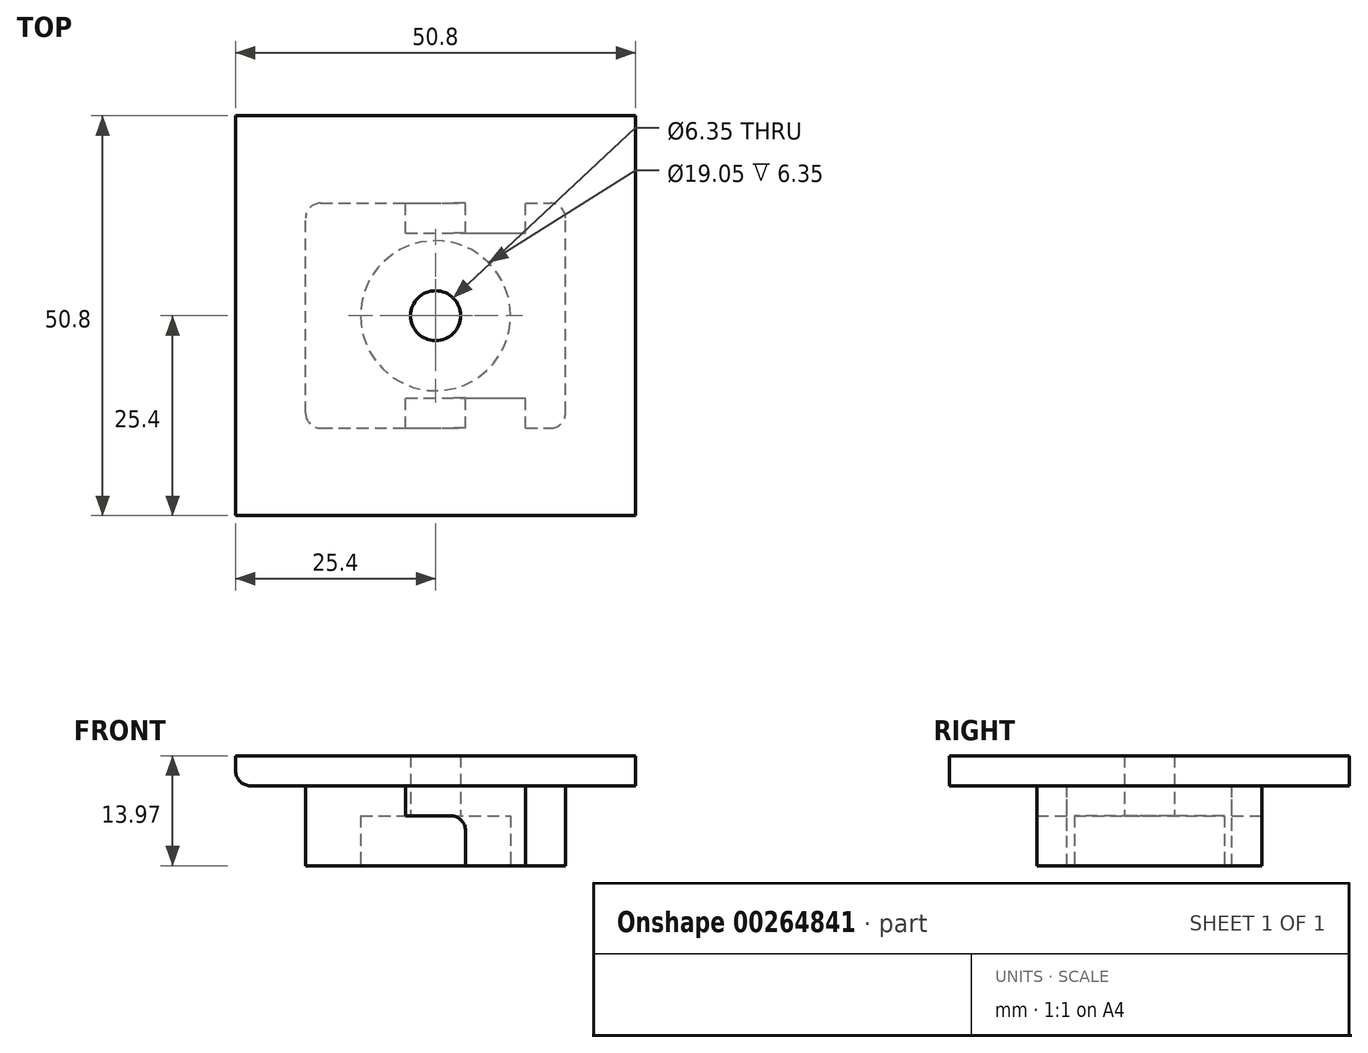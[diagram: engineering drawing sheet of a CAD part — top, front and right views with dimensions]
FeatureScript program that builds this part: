
annotation { "Feature Type Name" : "Feature", "Feature Type Description" : "" }
export const myFeature = defineFeature(function(context is Context, id is Id, definition is map)
    precondition{}
    {
        {
            var Q0;
            Q0=qCreatedBy(makeId("Top.planeOp"),FACE);
            var sketch = newSketch(context, id + "F0", { "sketchPlane" : qUnion([Q0])});
            skLineSegment(sketch, "E0.bottom", {"start": v(-25.4, 25.4) * mm, "end": v(25.4, 25.4) * mm});
            skLineSegment(sketch, "E0.top", {"start": v(-25.4, -25.4) * mm, "end": v(25.4, -25.4) * mm});
            skLineSegment(sketch, "E0.left", {"start": v(-25.4, 25.4) * mm, "end": v(-25.4, -25.4) * mm});
            skLineSegment(sketch, "E0.right", {"start": v(25.4, 25.4) * mm, "end": v(25.4, -25.4) * mm});
            skLineSegment(sketch, "E1", {"start": v(-25.4, 0) * mm, "end": v(25.4, 0) * mm, "construction": true});
            skSolve(sketch);
        }
        {
            var Q0;
            Q0 = qSketchRegion(id + "F0", true);
            extrude(context, id + "F1", {"entities" : qUnion([Q0]), "depth" : 3.8 * mm});
        }
        {
            var Q0;
            Q0=makeQuery(id+"F1.opExtrude","CAP_FACE",FACE,{"disambiguationData":[OSD([sQuery(id+"F0.wireOp",EDGE,"E0.bottom"),sQuery(id+"F0.wireOp",EDGE,"E0.top"),sQuery(id+"F0.wireOp",EDGE,"E0.left"),sQuery(id+"F0.wireOp",EDGE,"E0.right")])],"isStart":true});
            var sketch = newSketch(context, id + "F2", { "sketchPlane" : qUnion([Q0])});
            skLineSegment(sketch, "E2.bottom", {"start": v(-16.51, 14.29) * mm, "end": v(-3.81, 14.29) * mm});
            skLineSegment(sketch, "E2.top", {"start": v(-16.51, -14.29) * mm, "end": v(-3.81, -14.29) * mm});
            skLineSegment(sketch, "E2.left", {"start": v(-16.51, 14.29) * mm, "end": v(-16.51, -14.29) * mm});
            skLineSegment(sketch, "E2.right", {"start": v(16.51, 14.29) * mm, "end": v(16.51, -14.29) * mm});
            skLineSegment(sketch, "E3", {"start": v(-16.51, 0) * mm, "end": v(16.51, 0) * mm, "construction": true});
            skLineSegment(sketch, "E4", {"start": v(11.43, 14.29) * mm, "end": v(11.43, 10.48) * mm});
            skLineSegment(sketch, "E5", {"start": v(-3.81, 14.29) * mm, "end": v(-3.81, 10.48) * mm});
            skLineSegment(sketch, "E6", {"start": v(-3.81, 10.48) * mm, "end": v(11.43, 10.48) * mm});
            skLineSegment(sketch, "E7", {"start": v(-3.81, -10.48) * mm, "end": v(11.43, -10.48) * mm});
            skLineSegment(sketch, "E8.trimOffspring", {"start": v(-3.81, -10.48) * mm, "end": v(-3.81, -14.29) * mm});
            skLineSegment(sketch, "E9.trimOffspring", {"start": v(11.43, -10.48) * mm, "end": v(11.43, -14.29) * mm});
            skLineSegment(sketch, "E10.trimOffspring", {"start": v(11.43, -14.29) * mm, "end": v(16.51, -14.29) * mm});
            skLineSegment(sketch, "E11.trimOffspring", {"start": v(11.43, 14.29) * mm, "end": v(16.51, 14.29) * mm});
            skSolve(sketch);
        }
        {
            var Q0;
            Q0 = qSketchRegion(id + "F2", true);
            extrude(context, id + "F3", {"entities" : qUnion([Q0]), "operationType" : NewBodyOperationType.ADD, "depth" : 3.8 * mm});
        }
        {
            var Q0;
            Q0=makeQuery(id+"F3.opExtrude","CAP_FACE",FACE,{"disambiguationData":[OSD([sQuery(id+"F2.wireOp",EDGE,"E2.bottom"),sQuery(id+"F2.wireOp",EDGE,"E2.top"),sQuery(id+"F2.wireOp",EDGE,"E2.left"),sQuery(id+"F2.wireOp",EDGE,"E2.right"),sQuery(id+"F2.wireOp",EDGE,"E4"),sQuery(id+"F2.wireOp",EDGE,"E5"),sQuery(id+"F2.wireOp",EDGE,"E6"),sQuery(id+"F2.wireOp",EDGE,"E7"),sQuery(id+"F2.wireOp",EDGE,"E8.trimOffspring"),sQuery(id+"F2.wireOp",EDGE,"E9.trimOffspring"),sQuery(id+"F2.wireOp",EDGE,"E10.trimOffspring"),sQuery(id+"F2.wireOp",EDGE,"E11.trimOffspring")])],"isStart":false});
            var sketch = newSketch(context, id + "F4", { "sketchPlane" : qUnion([Q0])});
            skLineSegment(sketch, "E12.bottom", {"start": v(-16.51, 14.29) * mm, "end": v(3.81, 14.29) * mm});
            skLineSegment(sketch, "E12.top", {"start": v(-16.51, -14.29) * mm, "end": v(3.81, -14.29) * mm});
            skLineSegment(sketch, "E12.left", {"start": v(-16.51, 14.29) * mm, "end": v(-16.51, -14.29) * mm});
            skLineSegment(sketch, "E12.right", {"start": v(16.51, 14.29) * mm, "end": v(16.51, -14.29) * mm});
            skLineSegment(sketch, "E13", {"start": v(3.81, 14.29) * mm, "end": v(3.81, 10.48) * mm});
            skPoint(sketch, "E13.endSnap0", {"position": v(0, -14.29) * mm});
            skLineSegment(sketch, "E14", {"start": v(3.81, 10.48) * mm, "end": v(11.43, 10.48) * mm});
            skLineSegment(sketch, "E15", {"start": v(11.43, 10.48) * mm, "end": v(11.43, 14.29) * mm});
            skLineSegment(sketch, "E16", {"start": v(3.81, -10.48) * mm, "end": v(11.43, -10.48) * mm});
            skLineSegment(sketch, "E17", {"start": v(11.43, -10.48) * mm, "end": v(11.43, -14.29) * mm});
            skLineSegment(sketch, "E18.trimOffspring", {"start": v(11.43, 14.29) * mm, "end": v(16.51, 14.29) * mm});
            skLineSegment(sketch, "E19.trimOffspring", {"start": v(3.81, -10.48) * mm, "end": v(3.81, -14.29) * mm});
            skLineSegment(sketch, "E20.trimOffspring", {"start": v(11.43, -14.29) * mm, "end": v(16.51, -14.29) * mm});
            skSolve(sketch);
        }
        {
            var Q0;
            Q0 = qSketchRegion(id + "F4", true);
            extrude(context, id + "F5", {"entities" : qUnion([Q0]), "operationType" : NewBodyOperationType.ADD, "depth" : 6.35 * mm});
        }
        {
            var Q0;
            Q0=makeQuery(id+"F5.opExtrude","CAP_EDGE",EDGE,{"disambiguationData":[OSD([sQuery(id+"F4.wireOp",EDGE,"E13")])],"isStart":true});
            var Q1;
            Q1=makeQuery(id+"F5.boolean.opBoolean","MERGE",EDGE,{"derivedFrom":[makeQuery(id+"F3.opExtrude","SWEPT_EDGE",EDGE,{"disambiguationData":[OSD([sQuery(id+"F2.wireOp",EDGE,"E2.right"),sQuery(id+"F2.wireOp",EDGE,"E11.trimOffspring")])]}),makeQuery(id+"F5.opExtrude","SWEPT_EDGE",EDGE,{"disambiguationData":[OSD([sQuery(id+"F4.wireOp",EDGE,"E12.right"),sQuery(id+"F4.wireOp",EDGE,"E18.trimOffspring")])]})]});
            var Q2;
            Q2=makeQuery(id+"F5.boolean.opBoolean","MERGE",EDGE,{"derivedFrom":[makeQuery(id+"F3.opExtrude","SWEPT_EDGE",EDGE,{"disambiguationData":[OSD([sQuery(id+"F2.wireOp",EDGE,"E2.right"),sQuery(id+"F2.wireOp",EDGE,"E10.trimOffspring")])]}),makeQuery(id+"F5.opExtrude","SWEPT_EDGE",EDGE,{"disambiguationData":[OSD([sQuery(id+"F4.wireOp",EDGE,"E12.right"),sQuery(id+"F4.wireOp",EDGE,"E20.trimOffspring")])]})]});
            var Q3;
            Q3=makeQuery(id+"F5.opExtrude","CAP_EDGE",EDGE,{"disambiguationData":[OSD([sQuery(id+"F4.wireOp",EDGE,"E19.trimOffspring")])],"isStart":true});
            var Q4;
            Q4=makeQuery(id+"F5.boolean.opBoolean","MERGE",EDGE,{"derivedFrom":[makeQuery(id+"F3.opExtrude","SWEPT_EDGE",EDGE,{"disambiguationData":[OSD([sQuery(id+"F2.wireOp",EDGE,"E2.top"),sQuery(id+"F2.wireOp",EDGE,"E2.left")])]}),makeQuery(id+"F5.opExtrude","SWEPT_EDGE",EDGE,{"disambiguationData":[OSD([sQuery(id+"F4.wireOp",EDGE,"E12.top"),sQuery(id+"F4.wireOp",EDGE,"E12.left")])]})]});
            var Q5;
            Q5=makeQuery(id+"F5.boolean.opBoolean","MERGE",EDGE,{"derivedFrom":[makeQuery(id+"F3.opExtrude","SWEPT_EDGE",EDGE,{"disambiguationData":[OSD([sQuery(id+"F2.wireOp",EDGE,"E2.bottom"),sQuery(id+"F2.wireOp",EDGE,"E2.left")])]}),makeQuery(id+"F5.opExtrude","SWEPT_EDGE",EDGE,{"disambiguationData":[OSD([sQuery(id+"F4.wireOp",EDGE,"E12.bottom"),sQuery(id+"F4.wireOp",EDGE,"E12.left")])]})]});
            var Q6;
            Q6=makeQuery(id+"F1.opExtrude","CAP_EDGE",EDGE,{"disambiguationData":[OSD([sQuery(id+"F0.wireOp",EDGE,"E0.left")])],"isStart":true});
            fillet(context, id + "F6", {"entities" : qUnion([Q0, Q1, Q2, Q3, Q4, Q5, Q6]), "radius" : 1.9 * mm, "allowEdgeOverflow" : false});
        }
        {
            var Q0;
            Q0=makeQuery(id+"F5.opExtrude","CAP_FACE",FACE,{"disambiguationData":[OSD([sQuery(id+"F4.wireOp",EDGE,"E12.bottom"),sQuery(id+"F4.wireOp",EDGE,"E12.top"),sQuery(id+"F4.wireOp",EDGE,"E12.left"),sQuery(id+"F4.wireOp",EDGE,"E12.right"),sQuery(id+"F4.wireOp",EDGE,"E13"),sQuery(id+"F4.wireOp",EDGE,"E14"),sQuery(id+"F4.wireOp",EDGE,"E15"),sQuery(id+"F4.wireOp",EDGE,"E16"),sQuery(id+"F4.wireOp",EDGE,"E17"),sQuery(id+"F4.wireOp",EDGE,"E18.trimOffspring"),sQuery(id+"F4.wireOp",EDGE,"E19.trimOffspring"),sQuery(id+"F4.wireOp",EDGE,"E20.trimOffspring")])],"isStart":false});
            var sketch = newSketch(context, id + "F7", { "sketchPlane" : qUnion([Q0])});
            skPoint(sketch, "E21", {"position": v(0, 0) * mm});
            skSolve(sketch);
        }
        {
            var Q0;
            Q0=sQuery(id+"F7.wireOp",VERTEX,"E21");
            var Q1;
            Q1=makeQuery(id+"F1.opExtrude","SWEPT_BODY",BODY,{"disambiguationData":[OSD([sQuery(id+"F0.wireOp",EDGE,"E0.bottom"),sQuery(id+"F0.wireOp",EDGE,"E0.top"),sQuery(id+"F0.wireOp",EDGE,"E0.left"),sQuery(id+"F0.wireOp",EDGE,"E0.right")])]});
            hole(context, id + "F8", {"style" : HoleStyle.C_BORE, "endStyle" : HoleEndStyle.THROUGH, "holeDiameter" : 6.35 * mm, "cBoreDiameter" : 19.05 * mm, "cBoreDepth" : 6.35 * mm, "tappedDepth" : 12.7 * mm, "tapClearance" : 3, "startFromSketch" : true, "locations" : qUnion([Q0]), "scope" : qUnion([Q1])});
        }
    });
